# Revit family: STH8905BR_30_40_50_STH8905PTO_30_40
name_source: partatom
category: Luminárias
units: mm (PartAtom-declared; Revit-internal decimal feet)

## family parameters
Compartilhado = Não
Corte com vazios quando carregada = Não
Cota do conector redondo = Utilizar diâmetro
Fonte luminosa = Sim
Hospedeiro = Forro
Manter orientação da anotação = Não
Número OmniClass = 23.80.70.11
Ponto de cálculo do ambiente = Não
Sempre na vertical = Sim
Tipo de parte = Normal
Título OmniClass = Luminaries for Internal Lighting

## types (5) — shared parameters
Altura = 0.05 m
Comprimento = 0.35 m
Dimerização = Não dimerizável
Engate = Azul Stella
Fabricante = Stella
Filtro de cor = 16777215
Grau de proteção (IP) = IP20
IRC (Índice de reprodução de cores) = >80
Largura = 0.35 m
Modelo = Deep
Potência = 28 W
Tensão Elétrica = 100V-240V
Troca de temperatura da cor de lâmpada com esmaecimento = <Nenhum>
URL = https://stella.com.br
Ângulo de Abertura = 120°
Ângulo de inclinação = 90.00°
zero-valued in all types: Elevação padrão

## per-type parameters (varying)
| type | Arquivo de rede fotométrica | Estrutura | Fluxo Luminoso | Luminoso | Referência | Temperatura da cor (K) |
| STH8905BR/30 - BRANCO - BIVOLT - 3000K - 2450lm - 120° | STELLA - STH8905BR-30 - DEEP 30W.ies | Al - Branco | 2450 lm | Luminoso - 3000K | STH8905BR/30 - BRANCO - BIVOLT | 3000 K |
| STH8905PTO/30 - PRETO - BIVOLT - 3000K - 2100lm - 120° | STELLA - STH8905PTO-30 - PAINEL DEEP 30W.ies | Al - Preto | 2100 lm | Luminoso - 3000K | STH8905PTO/30 - PRETO - BIVOLT | 3000 K |
| STH8905BR/40 - BRANCO - BIVOLT - 4000K - 2500lm - 120° | STELLA - STH8905BR-40 - DEEP 30W.ies | Al - Branco | 2500 lm | Luminoso - 4000K | STH8905BR/40 - BRANCO - BIVOLT | 4000 K |
| STH8905PTO/40 - PRETO - BIVOLT - 4000K - 2150lm - 120° | STELLA - STH8905PTO-40 - PAINEL DEEP 30W.ies | Al - Preto | 2150 lm | Luminoso - 4000K | STH8905PTO/40 - PRETO - BIVOLT | 4000 K |
| STH8905BR/50 - BRANCO - BIVOLT - 5000K - 2550lm - 120° | STELLA - STH8905BR-50 - DEEP 30W.ies | Al - Branco | 2550 lm | Luminoso - 5000K | STH8905BR/50 - BRANCO - BIVOLT | 5000 K |
